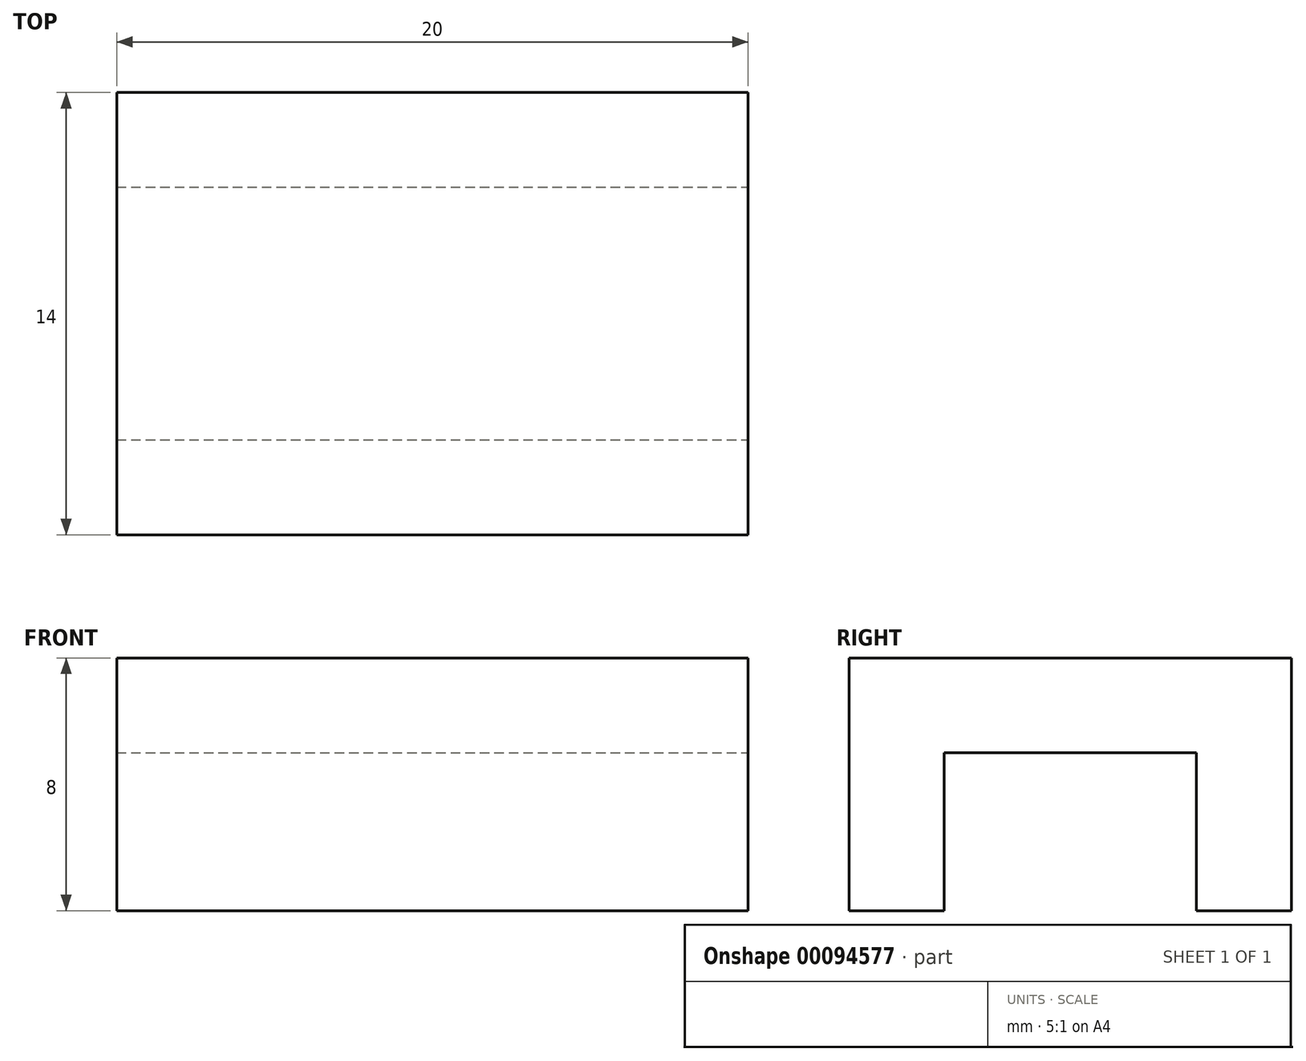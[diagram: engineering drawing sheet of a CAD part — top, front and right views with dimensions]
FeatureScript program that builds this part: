
annotation { "Feature Type Name" : "Feature", "Feature Type Description" : "" }
export const myFeature = defineFeature(function(context is Context, id is Id, definition is map)
    precondition{}
    {
        {
            var Q0;
            Q0=qCreatedBy(makeId("Front.planeOp"),FACE);
            var sketch = newSketch(context, id + "F0", { "sketchPlane" : qUnion([Q0])});
            skLineSegment(sketch, "E0", {"start": v(-32, 0) * mm, "end": v(0, 0) * mm, "construction": true});
            skArc(sketch, "E1.0.startCap", {"start": v(-32, -8) * mm, "mid": v(-40, 0) * mm, "end": v(-32, 8) * mm});
            skArc(sketch, "E1.0.endCap", {"start": v(0, 8) * mm, "mid": v(8, 0) * mm, "end": v(0, -8) * mm});
            skLineSegment(sketch, "E1.0.left", {"start": v(-32, 8) * mm, "end": v(0, 8) * mm});
            skLineSegment(sketch, "E1.0.right", {"start": v(-32, -8) * mm, "end": v(0, -8) * mm});
            skCircle(sketch, "E2", {"center": v(-32, 0) * mm, "radius": 3 * mm});
            skCircle(sketch, "E3.1.0.0", {"center": v(0, 0) * mm, "radius": 3 * mm});
            skLineSegment(sketch, "E4.bottom", {"start": v(-20, 16) * mm, "end": v(0, 16) * mm});
            skLineSegment(sketch, "E4.top", {"start": v(-20, 8) * mm, "end": v(0, 8) * mm});
            skLineSegment(sketch, "E4.left", {"start": v(-20, 16) * mm, "end": v(-20, 8) * mm});
            skLineSegment(sketch, "E4.right", {"start": v(0, 16) * mm, "end": v(0, 8) * mm});
            skSolve(sketch);
        }
        {
            var Q0;
            Q0=makeQuery(id+"F0.imprint","IMPRINT",FACE,{"disambiguationData":[TD([[makeQuery(id+"F0.imprint","IMPRINT",EDGE,{"derivedFrom":sQuery(id+"F0.wireOp",EDGE,"E4.bottom")}),-1.0]])]});
            var Q1;
            Q1=makeQuery(id+"F0.imprint","IMPRINT",FACE,{"disambiguationData":[TD([[makeQuery(id+"F0.imprint","IMPRINT",EDGE,{"derivedFrom":sQuery(id+"F0.wireOp",EDGE,"E1.0.startCap")}),-1.0]])]});
            extrude(context, id + "F1", {"entities" : qUnion([Q0, Q1]), "endBound" : BoundingType.SYMMETRIC, "depth" : 14 * mm});
        }
        {
            var Q0;
            Q0=qCreatedBy(makeId("Right.planeOp"),FACE);
            var sketch = newSketch(context, id + "F2", { "sketchPlane" : qUnion([Q0])});
            skLineSegment(sketch, "E5.bottom", {"start": v(4, 13) * mm, "end": v(-4, 13) * mm});
            skLineSegment(sketch, "E5.top", {"start": v(4, -13) * mm, "end": v(-4, -13) * mm});
            skLineSegment(sketch, "E5.left", {"start": v(4, 13) * mm, "end": v(4, -13) * mm});
            skLineSegment(sketch, "E5.right", {"start": v(-4, 13) * mm, "end": v(-4, -13) * mm});
            skPoint(sketch, "E5.middle", {"position": v(0, 0) * mm});
            skSolve(sketch);
        }
        {
            var Q0;
            Q0=makeQuery(id+"F2.imprint","IMPRINT",FACE,{"disambiguationData":[TD([[makeQuery(id+"F2.imprint","IMPRINT",EDGE,{"derivedFrom":sQuery(id+"F2.wireOp",EDGE,"E5.bottom")}),1.0]])]});
            extrude(context, id + "F3", {"entities" : qUnion([Q0]), "operationType" : NewBodyOperationType.REMOVE, "endBound" : BoundingType.SYMMETRIC, "oppositeDirection" : true, "depth" : 151.7 * mm});
        }
    });
